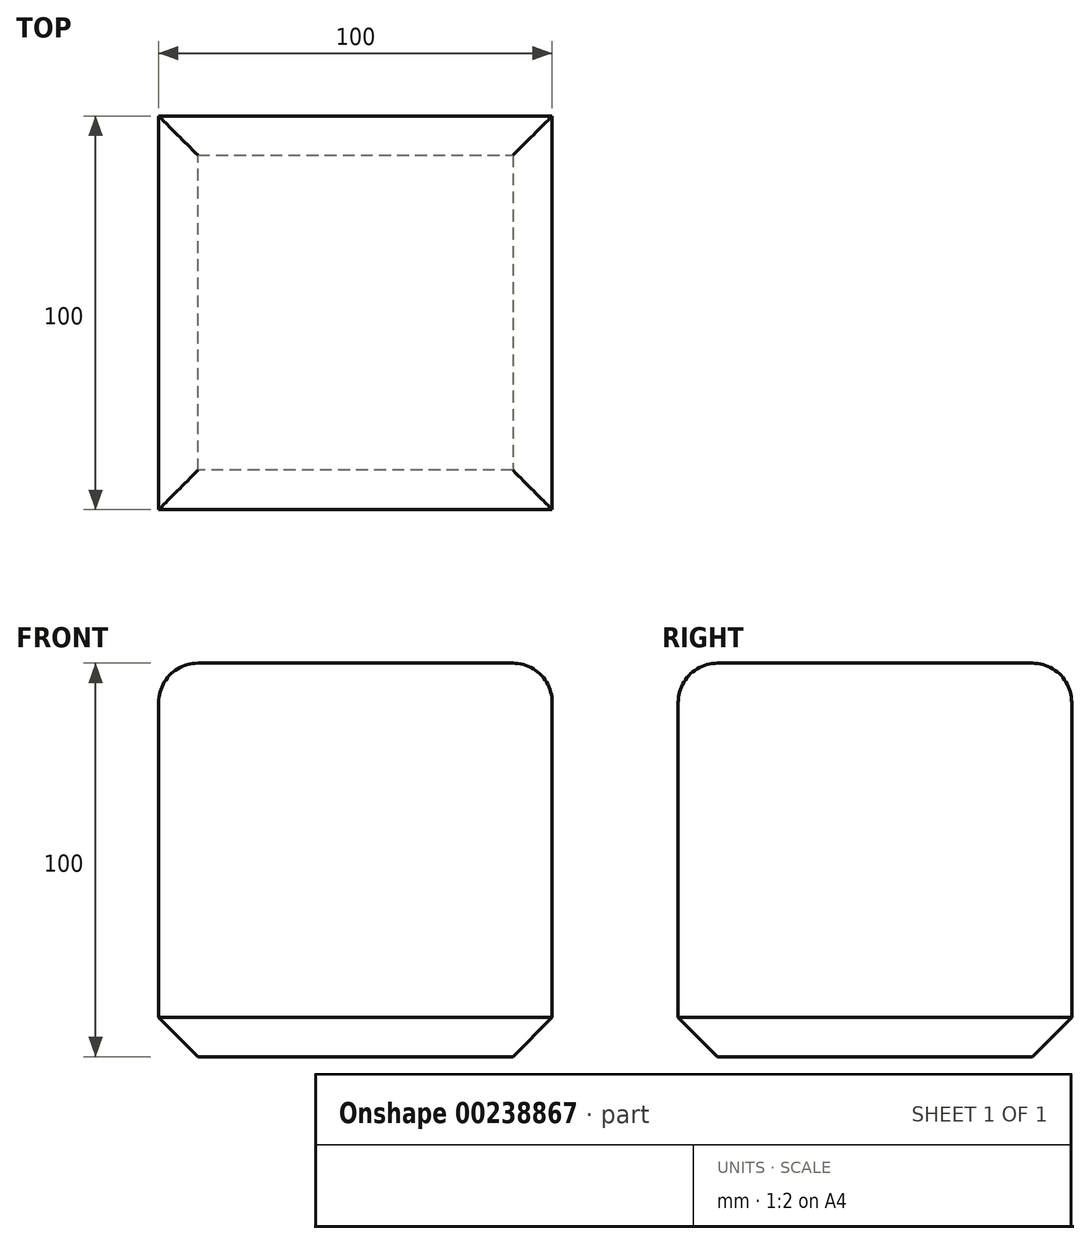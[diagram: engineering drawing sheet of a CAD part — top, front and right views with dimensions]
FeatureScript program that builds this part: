
annotation { "Feature Type Name" : "Feature", "Feature Type Description" : "" }
export const myFeature = defineFeature(function(context is Context, id is Id, definition is map)
    precondition{}
    {
        {
            var Q0;
            Q0=qCreatedBy(makeId("Top.planeOp"),FACE);
            var sketch = newSketch(context, id + "F0", { "sketchPlane" : qUnion([Q0])});
            skLineSegment(sketch, "E0.bottom", {"start": v(-50, 50) * mm, "end": v(50, 50) * mm});
            skLineSegment(sketch, "E0.top", {"start": v(-50, -50) * mm, "end": v(50, -50) * mm});
            skLineSegment(sketch, "E0.left", {"start": v(-50, 50) * mm, "end": v(-50, -50) * mm});
            skLineSegment(sketch, "E0.right", {"start": v(50, 50) * mm, "end": v(50, -50) * mm});
            skSolve(sketch);
        }
        {
            var Q0;
            Q0 = qSketchRegion(id + "F0", true);
            extrude(context, id + "F1", {"entities" : qUnion([Q0]), "depth" : 100 * mm});
        }
        {
            var Q0;
            Q0=makeQuery(id+"F1.opExtrude","CAP_FACE",FACE,{"disambiguationData":[OSD([sQuery(id+"F0.wireOp",EDGE,"E0.bottom"),sQuery(id+"F0.wireOp",EDGE,"E0.top"),sQuery(id+"F0.wireOp",EDGE,"E0.left"),sQuery(id+"F0.wireOp",EDGE,"E0.right")])],"isStart":false});
            fillet(context, id + "F2", {"entities" : qUnion([Q0]), "radius" : 10 * mm, "tangentPropagation" : true, "allowEdgeOverflow" : false});
        }
        {
            var Q0;
            Q0=makeQuery(id+"F1.opExtrude","CAP_FACE",FACE,{"disambiguationData":[OSD([sQuery(id+"F0.wireOp",EDGE,"E0.bottom"),sQuery(id+"F0.wireOp",EDGE,"E0.top"),sQuery(id+"F0.wireOp",EDGE,"E0.left"),sQuery(id+"F0.wireOp",EDGE,"E0.right")])],"isStart":true});
            chamfer(context, id + "F3", {"entities" : qUnion([Q0]), "width" : 10 * mm, "tangentPropagation" : true});
        }
    });
